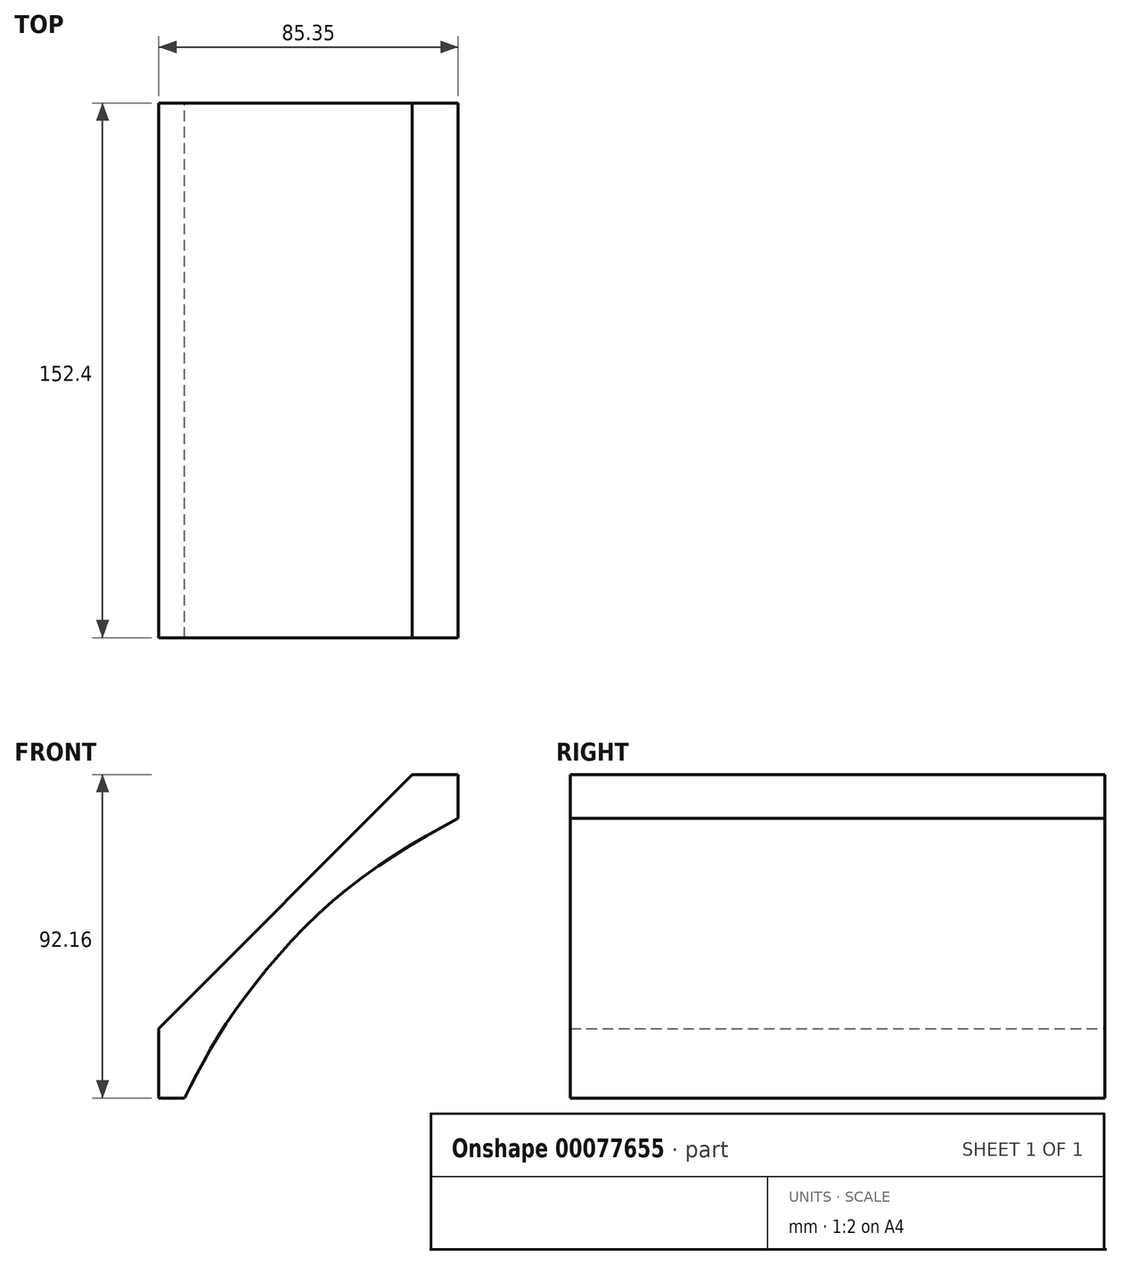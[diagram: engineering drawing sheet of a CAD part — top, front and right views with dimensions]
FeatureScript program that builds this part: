
annotation { "Feature Type Name" : "Feature", "Feature Type Description" : "" }
export const myFeature = defineFeature(function(context is Context, id is Id, definition is map)
    precondition{}
    {
        {
            var Q0;
            Q0=qCreatedBy(makeId("Front.planeOp"),FACE);
            var sketch = newSketch(context, id + "F0", { "sketchPlane" : qUnion([Q0])});
            skLineSegment(sketch, "E0", {"start": v(-35.26, -46.06) * mm, "end": v(-42.66, -46.06) * mm});
            skLineSegment(sketch, "E1", {"start": v(-42.66, -46.06) * mm, "end": v(-42.66, -26.26) * mm});
            skLineSegment(sketch, "E2", {"start": v(-42.66, -26.26) * mm, "end": v(29.57, 46.1) * mm});
            skLineSegment(sketch, "E3", {"start": v(29.57, 46.1) * mm, "end": v(42.68, 46.1) * mm});
            skLineSegment(sketch, "E4", {"start": v(42.68, 46.1) * mm, "end": v(42.7, 33.7) * mm});
            skFitSpline(sketch, "E5", {"points": [v(-35.26, -46.06) * mm, v(-28.5, -33.13) * mm, v(-18.6, -17.98) * mm, v(-1.66, 1.93) * mm, v(19.78, 20) * mm, v(42.7, 33.7) * mm], "startDerivative": vector(39.73, 79.57) * mm, "endDerivative": vector(106.44, 58.95) * mm});
            skSolve(sketch);
        }
        {
            var Q0;
            Q0=makeQuery(id+"F0.imprint","IMPRINT",FACE,{"disambiguationData":[TD([[makeQuery(id+"F0.imprint","IMPRINT",EDGE,{"derivedFrom":sQuery(id+"F0.wireOp",EDGE,"E0")}),-1.0]])]});
            extrude(context, id + "F1", {"entities" : qUnion([Q0]), "depth" : 152.4 * mm});
        }
    });
